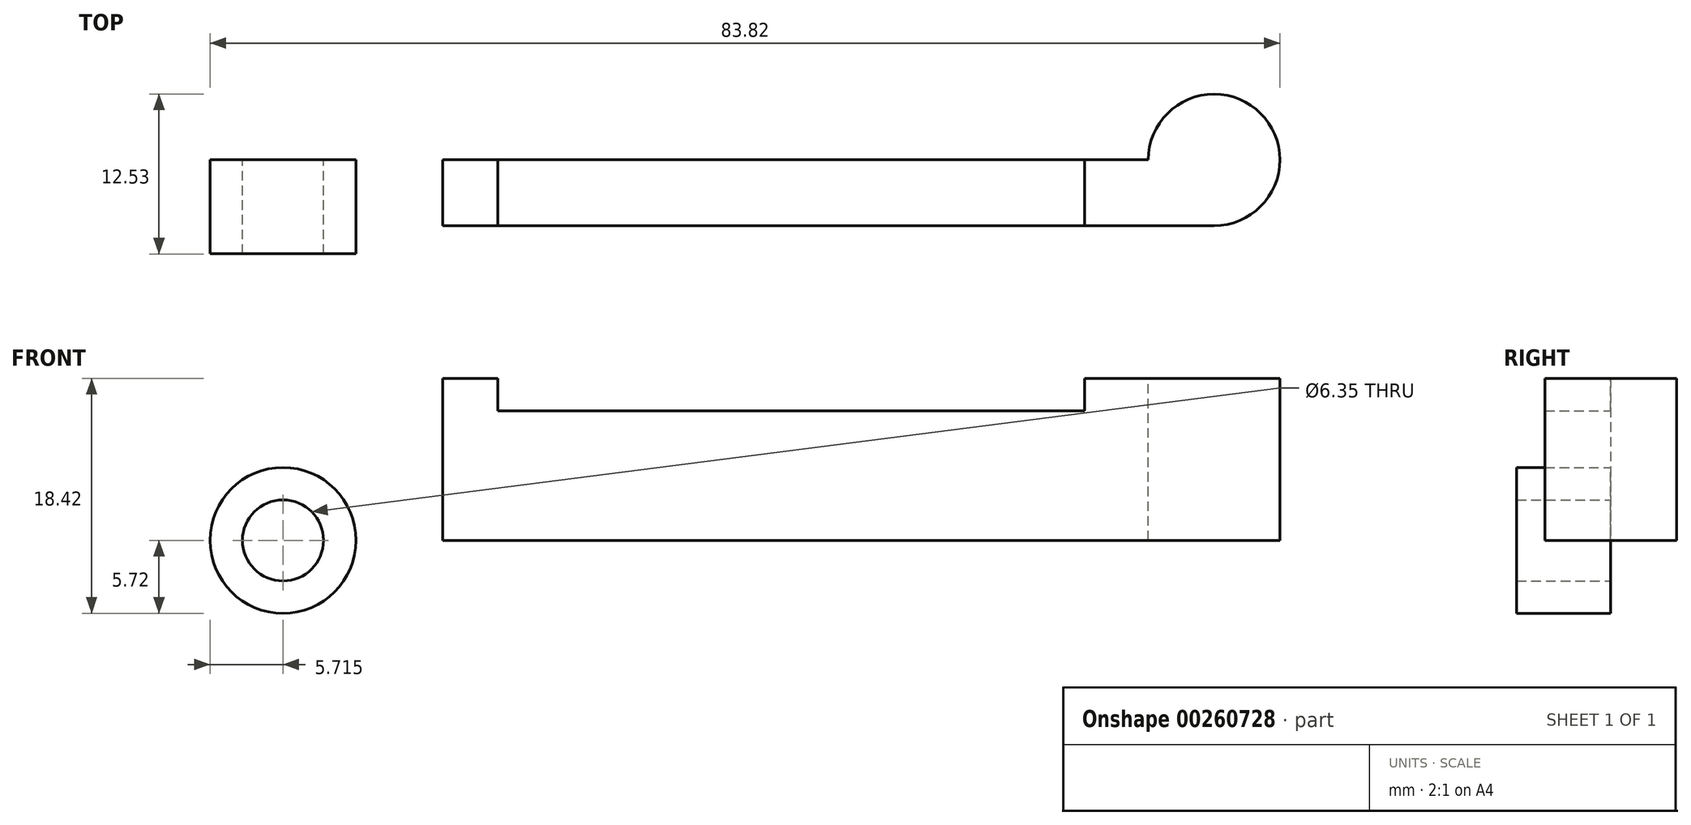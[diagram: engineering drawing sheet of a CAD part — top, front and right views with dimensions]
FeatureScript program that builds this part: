
annotation { "Feature Type Name" : "Feature", "Feature Type Description" : "" }
export const myFeature = defineFeature(function(context is Context, id is Id, definition is map)
    precondition{}
    {
        {
            var Q0;
            Q0=qCreatedBy(makeId("Front.planeOp"),FACE);
            var sketch = newSketch(context, id + "F0", { "sketchPlane" : qUnion([Q0])});
            skLineSegment(sketch, "E0", {"start": v(0, 0) * mm, "end": v(0, 12.7) * mm});
            skLineSegment(sketch, "E1", {"start": v(0, 12.7) * mm, "end": v(10.16, 12.7) * mm});
            skLineSegment(sketch, "E2", {"start": v(10.16, 12.7) * mm, "end": v(10.16, 10.16) * mm});
            skLineSegment(sketch, "E3", {"start": v(10.16, 10.16) * mm, "end": v(56.13, 10.16) * mm});
            skLineSegment(sketch, "E4", {"start": v(56.13, 10.16) * mm, "end": v(56.13, 12.7) * mm});
            skLineSegment(sketch, "E5", {"start": v(56.13, 12.7) * mm, "end": v(66.3, 12.7) * mm});
            skLineSegment(sketch, "E6", {"start": v(66.3, 12.7) * mm, "end": v(66.3, 0) * mm});
            skLineSegment(sketch, "E7", {"start": v(66.3, 0) * mm, "end": v(0, 0) * mm});
            skLineSegment(sketch, "E8", {"start": v(5.84, 15.24) * mm, "end": v(-0.5, 15.24) * mm});
            skLineSegment(sketch, "E9", {"start": v(-0.5, 15.24) * mm, "end": v(-10.88, 3.85) * mm});
            skLineSegment(sketch, "E10", {"start": v(0, 0) * mm, "end": v(-6.65, 0) * mm});
            skCircle(sketch, "E11", {"center": v(-6.65, 0) * mm, "radius": 5.72 * mm});
            skCircle(sketch, "E12", {"center": v(-6.65, 0) * mm, "radius": 3.18 * mm});
            skLineSegment(sketch, "E13", {"start": v(5.84, 15.24) * mm, "end": v(5.84, -9.4) * mm});
            skLineSegment(sketch, "E14", {"start": v(5.84, -9.4) * mm, "end": v(-8.18, -5.5) * mm});
            skSolve(sketch);
        }
        {
            var Q0;
            {var subQ0=sQuery(id+"F0.wireOp",EDGE,"E2");Q0=makeQuery(id+"F0.imprint","IMPRINT",FACE,{"disambiguationData":[TD([[makeQuery(id+"F0.imprint","IMPRINT",EDGE,{"derivedFrom":subQ0}),-1.0]])]});}
            extrude(context, id + "F1", {"entities" : qUnion([Q0]), "depth" : 5.16 * mm});
        }
        {
            var Q0;
            {var subQ4=sQuery(id+"F0.wireOp",EDGE,"E12");Q0=makeQuery(id+"F0.imprint","IMPRINT",FACE,{"disambiguationData":[TD([[makeQuery(id+"F0.imprint","IMPRINT",EDGE,{"derivedFrom":subQ4}),-1.0]])]});}
            extrude(context, id + "F2", {"entities" : qUnion([Q0]), "depth" : 7.37 * mm});
        }
        {
            var Q0;
            Q0=makeQuery(id+"F1.opExtrude","SWEPT_FACE",FACE,{"disambiguationData":[OSD([sQuery(id+"F0.wireOp",EDGE,"E6")])]});
            var Q1;
            Q1=sQuery(id+"F0.wireOp",EDGE,"E6");
            revolve(context, id + "F3", {"operationType" : NewBodyOperationType.ADD, "entities" : qUnion([Q0]), "axis" : qUnion([Q1]), "revolveType" : RevolveType.FULL});
        }
    });
